# Revit family: TD-251_001CP
name_source: partatom
category: Plumbing Fixtures
revit_build: Autodesk Revit Architecture 2012 (Build: 20110309_2315(x64)
units: mm (PartAtom-declared; Revit-internal decimal feet)

## types (1)
- TD-251/001CP
    1/2" light pattern tap washer = C-098-15
    Assembly Code = D2010
    CW Connection = Yes
    CWFU = 0
    Cost = 0 $
    Default Elevation = 0' - 0"
    Description = Wall type with diverter and handshower attachment. 1/2"BSP male inlets
    HW Connection = Yes
    HWFU = 0
    Handshower = VIC-001/1CP
    Handshower cradle = VIC-CRADLE
    Handshower hose = 008/4C
    Headpart complete = P-62-1TD/CP
    Indice = VIC-INDIC/CP
    Indices = VIC-INDIC/CP
    Keynote = Wide sweep S-connections for easy retrofit
    Manufacturer = COBRA
    Material = Chrome - Polished
    Model = TD-251/001CP
    Range = Tudor
    Type Comments = SANS 226 TYPE 2
    URL = http://www.cobra.co.za
    Vent Connection = No
    WFU = 0
    Waste Connection = No

## geometry (parser evidence)
native form markers: Blend x2
no freeform markers — native parametric forms only
